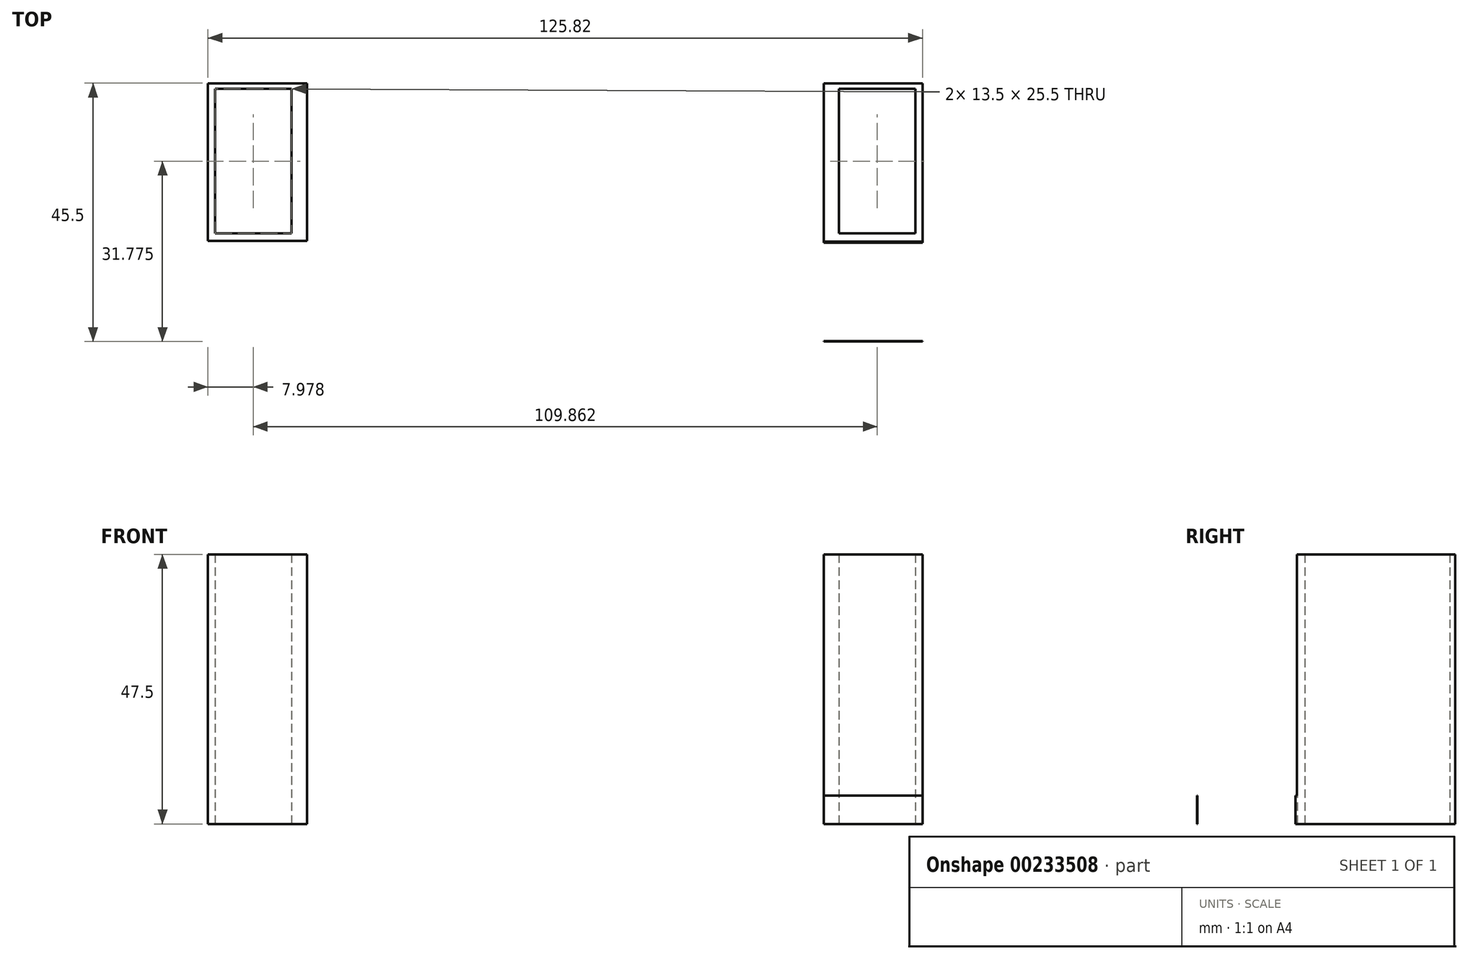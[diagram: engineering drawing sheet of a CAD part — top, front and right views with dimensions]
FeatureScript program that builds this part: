
annotation { "Feature Type Name" : "Feature", "Feature Type Description" : "" }
export const myFeature = defineFeature(function(context is Context, id is Id, definition is map)
    precondition{}
    {
        {
            var Q0;
            Q0=qCreatedBy(makeId("Top.planeOp"),FACE);
            var sketch = newSketch(context, id + "F0", { "sketchPlane" : qUnion([Q0])});
            skLineSegment(sketch, "E0.bottom", {"start": v(-11.78, 14.9) * mm, "end": v(1.72, 14.9) * mm});
            skLineSegment(sketch, "E0.top", {"start": v(-11.78, -10.6) * mm, "end": v(1.72, -10.6) * mm});
            skLineSegment(sketch, "E0.left", {"start": v(-11.78, 14.9) * mm, "end": v(-11.78, -10.6) * mm});
            skLineSegment(sketch, "E0.right", {"start": v(1.72, 14.9) * mm, "end": v(1.72, -10.6) * mm});
            skLineSegment(sketch, "E1.top", {"start": v(-13.01, -29.63) * mm, "end": v(4.4, -29.63) * mm});
            skLineSegment(sketch, "E1.left", {"start": v(-13.01, 15.87) * mm, "end": v(-13.01, -29.63) * mm});
            skLineSegment(sketch, "E1.right", {"start": v(4.4, 15.87) * mm, "end": v(4.4, -29.63) * mm});
            skLineSegment(sketch, "E2", {"start": v(4.4, 15.87) * mm, "end": v(-13.01, 15.87) * mm});
            skPoint(sketch, "E3.orphan", {"position": v(4.4, 17.86) * mm});
            skLineSegment(sketch, "E4", {"start": v(4.4, 15.87) * mm, "end": v(95.4, 15.87) * mm});
            skLineSegment(sketch, "E5", {"start": v(4.4, 15.87) * mm, "end": v(49.9, 15.87) * mm});
            skLineSegment(sketch, "E6.MirrorCS", {"start": v(95.4, 15.87) * mm, "end": v(95.4, -29.63) * mm});
            skLineSegment(sketch, "E7.MirrorCS", {"start": v(98.08, 14.9) * mm, "end": v(98.08, -10.6) * mm});
            skLineSegment(sketch, "E8.MirrorCS", {"start": v(111.58, -10.6) * mm, "end": v(98.08, -10.6) * mm});
            skLineSegment(sketch, "E9.MirrorCS", {"start": v(112.81, -29.63) * mm, "end": v(95.4, -29.63) * mm});
            skLineSegment(sketch, "E10.MirrorCS", {"start": v(111.58, 14.9) * mm, "end": v(111.58, -10.6) * mm});
            skLineSegment(sketch, "E11.MirrorCS", {"start": v(112.81, 15.87) * mm, "end": v(112.81, -29.63) * mm});
            skLineSegment(sketch, "E12.MirrorCS", {"start": v(95.4, 15.87) * mm, "end": v(112.81, 15.87) * mm});
            skLineSegment(sketch, "E13.MirrorCS", {"start": v(111.58, 14.9) * mm, "end": v(98.08, 14.9) * mm});
            skSolve(sketch);
        }
        {
            var Q0;
            Q0=makeQuery(id+"F0.imprint","IMPRINT",FACE,{"disambiguationData":[TD([[makeQuery(id+"F0.imprint","IMPRINT",EDGE,{"derivedFrom":sQuery(id+"F0.wireOp",EDGE,"E6.MirrorCS")}),1.0]])]});
            var Q1;
            Q1=makeQuery(id+"F0.imprint","IMPRINT",FACE,{"disambiguationData":[TD([[makeQuery(id+"F0.imprint","IMPRINT",EDGE,{"derivedFrom":sQuery(id+"F0.wireOp",EDGE,"E0.bottom")}),1.0]])]});
            extrude(context, id + "F1", {"entities" : qUnion([Q0, Q1]), "depth" : 47.5 * mm});
        }
        {
            var Q0;
            Q0=makeQuery(id+"F1.opExtrude","CAP_FACE",FACE,{"disambiguationData":[OSD([sQuery(id+"F0.wireOp",EDGE,"E0.bottom"),sQuery(id+"F0.wireOp",EDGE,"E0.top"),sQuery(id+"F0.wireOp",EDGE,"E0.left"),sQuery(id+"F0.wireOp",EDGE,"E0.right"),sQuery(id+"F0.wireOp",EDGE,"E1.top"),sQuery(id+"F0.wireOp",EDGE,"E1.left"),sQuery(id+"F0.wireOp",EDGE,"E1.right"),sQuery(id+"F0.wireOp",EDGE,"E2")])],"isStart":false});
            var sketch = newSketch(context, id + "F2", { "sketchPlane" : qUnion([Q0])});
            skLineSegment(sketch, "E14.bottom", {"start": v(-13.01, -29.63) * mm, "end": v(4.4, -29.63) * mm});
            skLineSegment(sketch, "E14.top", {"start": v(-13.01, -11.93) * mm, "end": v(4.4, -11.93) * mm});
            skLineSegment(sketch, "E14.left", {"start": v(-13.01, -29.63) * mm, "end": v(-13.01, -11.93) * mm});
            skLineSegment(sketch, "E14.right", {"start": v(4.4, -29.63) * mm, "end": v(4.4, -11.93) * mm});
            skLineSegment(sketch, "E15.bottom", {"start": v(95.3, -29.55) * mm, "end": v(112.8, -29.55) * mm});
            skLineSegment(sketch, "E15.top", {"start": v(95.3, -12.25) * mm, "end": v(112.8, -12.25) * mm});
            skLineSegment(sketch, "E15.left", {"start": v(95.3, -29.55) * mm, "end": v(95.3, -12.25) * mm});
            skLineSegment(sketch, "E15.right", {"start": v(112.8, -29.55) * mm, "end": v(112.8, -12.25) * mm});
            skSolve(sketch);
        }
        {
            var Q0;
            Q0=makeQuery(id+"F2.imprint","IMPRINT",FACE,{"disambiguationData":[TD([[makeQuery(id+"F2.imprint","IMPRINT",EDGE,{"derivedFrom":sQuery(id+"F2.wireOp",EDGE,"E15.bottom")}),1.0]])]});
            var Q1;
            Q1=makeQuery(id+"F2.imprint","IMPRINT",FACE,{"disambiguationData":[TD([[makeQuery(id+"F2.imprint","IMPRINT",EDGE,{"derivedFrom":sQuery(id+"F2.wireOp",EDGE,"E14.bottom")}),1.0]])]});
            extrude(context, id + "F3", {"entities" : qUnion([Q0, Q1]), "operationType" : NewBodyOperationType.REMOVE, "endBound" : BoundingType.THROUGH_ALL, "oppositeDirection" : true, "depth" : 42.5 * mm});
        }
        {
            var Q0;
            Q0=makeQuery(id+"F1.opExtrude","CAP_FACE",FACE,{"disambiguationData":[OSD([sQuery(id+"F0.wireOp",EDGE,"E0.bottom"),sQuery(id+"F0.wireOp",EDGE,"E0.top"),sQuery(id+"F0.wireOp",EDGE,"E0.left"),sQuery(id+"F0.wireOp",EDGE,"E0.right"),sQuery(id+"F0.wireOp",EDGE,"E1.top"),sQuery(id+"F0.wireOp",EDGE,"E1.left"),sQuery(id+"F0.wireOp",EDGE,"E1.right"),sQuery(id+"F0.wireOp",EDGE,"E2")])],"isStart":false});
            var sketch = newSketch(context, id + "F4", { "sketchPlane" : qUnion([Q0])});
            skLineSegment(sketch, "E16.bottom", {"start": v(-19.15, -12.04) * mm, "end": v(147.08, -12.04) * mm});
            skLineSegment(sketch, "E16.top", {"start": v(-19.15, -60.55) * mm, "end": v(147.08, -60.55) * mm});
            skLineSegment(sketch, "E16.left", {"start": v(-19.15, -12.04) * mm, "end": v(-19.15, -60.55) * mm});
            skLineSegment(sketch, "E16.right", {"start": v(147.08, -12.04) * mm, "end": v(147.08, -60.55) * mm});
            skSolve(sketch);
        }
        {
            var Q0;
            {var subQ5=makeQuery(id+"F1.opExtrude","CAP_EDGE",EDGE,{"disambiguationData":[OSD([sQuery(id+"F0.wireOp",EDGE,"E1.top")])],"isStart":false});Q0=makeQuery(id+"F4.imprint","IMPRINT",FACE,{"disambiguationData":[TD([[makeQuery(id+"F4.imprint","IMPRINT",EDGE,{"derivedFrom":subQ5}),1.0]])]});}
            var Q1;
            Q1=makeQuery(id+"F4.imprint","IMPRINT",FACE,{"disambiguationData":[TD([[makeQuery(id+"F4.imprint","IMPRINT",EDGE,{"derivedFrom":sQuery(id+"F4.wireOp",EDGE,"E16.top")}),1.0]])]});
            extrude(context, id + "F5", {"entities" : qUnion([Q0, Q1]), "operationType" : NewBodyOperationType.REMOVE, "oppositeDirection" : true, "depth" : 42.5 * mm});
        }
    });
